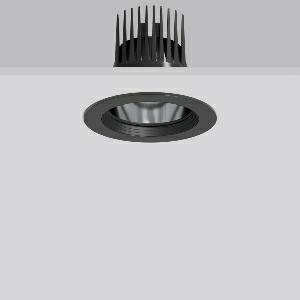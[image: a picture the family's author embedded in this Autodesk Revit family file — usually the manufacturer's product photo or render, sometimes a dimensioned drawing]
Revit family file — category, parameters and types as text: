
# Revit family: heledon_maxi_e_901765_003_76_e86c
name_source: partatom
category: Lighting Fixtures
units: mm (PartAtom-declared; Revit-internal decimal feet)

## family parameters
Cut with Voids When Loaded = No
Host = Face
Light Source = No
Part Type = Normal
Room Calculation Point = No
Round Connector Dimension = Use Diameter
Shared = No

## types (1)
- HELEDON maxi E (1 x LED Modul 930, 4350 lm, 3000)
    Apparent Load = 35 VA
    Approval mark = CE
    CIE Flux Codes = 100 100 100 100 100
    Color Rendering = 90
    Color Temperature = 3000
    Default Elevation = 1800 mm
    Description = Series: HELEDON maxi
Round recessed downlight. Housing: die-cast aluminium, powder-coated. Black plastic ring and recessed LED to prevent glare from the side. Optical assembly with reflector made of MIRO-Silver with 98% total light reflection for outstanding efficiency - can be changed without tools. Best colour rendering index Ra>90. Suitable for Recessed ceiling mounting. Installation without tools thanks to spring fastening system. Including separate LED converter with connecting cable 600 mm.High quality converter without flickering and stroboscopic effect. Through-wiring box (5 pole) available as accessory. The following accessories can be mounted without use of tools: interchangeable lenses, decorative glasses, honeycomb louvre, clear and frosted diffusers, white interchangeable plastic ring. 
Colour: deep black, matt (RAL 9005)
Diameter: 162 mm
Height: 3 mm
Cut-out diameter: 152 mm
Recess height: 200 mm
Luminaire: recess height: 135 mm
Lamp: LED
Socket: without socket
Colour temperature: 3000K
Colour rendering index (CRI): 92
System power: 35 W
Rated luminous flux: 4350 lm
Luminous efficiency: 124 lm/W
Control gear: Converter, dimmable, DALI
Protection class: II
Type of protection: IP 20
    Height = 0 mm  [stored 0 ft]
    Lamp = 1 x LED Modul 930
    Lamp Light Flux = 4350 lm
    Lamp count = 1
    Length = 162 mm
    Lifetime = 50000 h
    Luminous efficacy = 124 lm/W
    Manufacturer = RZB
    ModVariant = No
    Model = 901765.003.76
    Mounting Place = Ceiling
    Mounting Type = Recessed
    Number of Poles = 1
    OnlyDefault = Yes
    Power Factor = 1
    Product Name = HELEDON maxi E
    Product group = Recessed downlights
    ProductGroupID = 402
    Protection Class = Protection class II
    Protection Degree = IP 20
    RLX_Detail_Level = 1
    RLX_Emergency_Light_Flux = 0 lm
    RLX_Emergency_Type = 0
    RLX_Emergency_Type_DB = No
    RlxData = <blob elided: 121853 chars, md5=fb2d42c9>
    Socket = socket
    Standby Power = 0 W
    System Light Flux = 4350 lm
    System Power = 35 W
    Type Comments = Product without accessories
    Type Image = 901662.003.jpg
    URL = http://relux.com
    VarID = ---
    Voltage = 230 V
    Voltage Range = 220-240 V
    Weight = 0.00 kg
    Width = 0 mm  [stored 0 ft]

note: [stored X ft] marks values corroborated as IEEE doubles in the binary element streams (Revit-internal decimal feet)

## geometry (parser evidence)
native form markers: Blend x4, Sweep x10
no freeform markers — native parametric forms only
